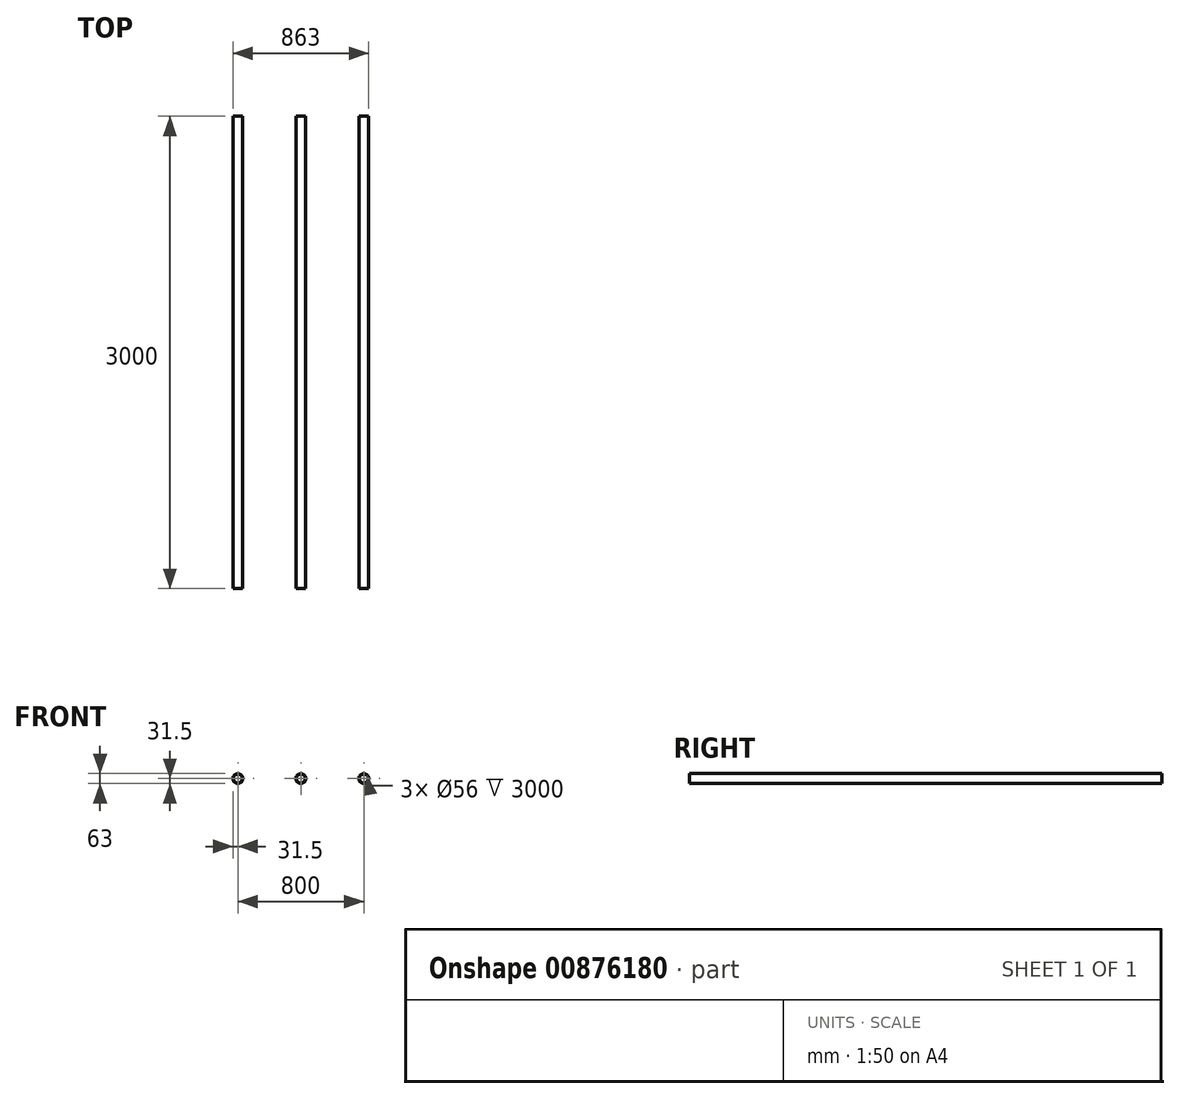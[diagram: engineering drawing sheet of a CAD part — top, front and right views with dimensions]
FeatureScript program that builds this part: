
annotation { "Feature Type Name" : "Feature", "Feature Type Description" : "" }
export const myFeature = defineFeature(function(context is Context, id is Id, definition is map)
    precondition{}
    {
        {
            var Q0;
            Q0=qCreatedBy(makeId("Front.planeOp"),FACE);
            var sketch = newSketch(context, id + "F0", { "sketchPlane" : qUnion([Q0])});
            skCircle(sketch, "E0", {"center": v(0, 0) * mm, "radius": 31.5 * mm});
            skCircle(sketch, "E1", {"center": v(0, 0) * mm, "radius": 28 * mm});
            skCircle(sketch, "E2", {"center": v(400, 0) * mm, "radius": 31.5 * mm});
            skCircle(sketch, "E3", {"center": v(400, 0) * mm, "radius": 28 * mm});
            skCircle(sketch, "E4", {"center": v(-400, 0) * mm, "radius": 31.5 * mm});
            skCircle(sketch, "E5", {"center": v(-400, 0) * mm, "radius": 28 * mm});
            skSolve(sketch);
        }
        {
            var Q0;
            Q0=makeQuery(id+"F0.imprint","IMPRINT",FACE,{"disambiguationData":[TD([[makeQuery(id+"F0.imprint","IMPRINT",EDGE,{"derivedFrom":sQuery(id+"F0.wireOp",EDGE,"E4")}),1.0]])]});
            var Q1;
            Q1=makeQuery(id+"F0.imprint","IMPRINT",FACE,{"disambiguationData":[TD([[makeQuery(id+"F0.imprint","IMPRINT",EDGE,{"derivedFrom":sQuery(id+"F0.wireOp",EDGE,"E0")}),1.0]])]});
            var Q2;
            Q2=makeQuery(id+"F0.imprint","IMPRINT",FACE,{"disambiguationData":[TD([[makeQuery(id+"F0.imprint","IMPRINT",EDGE,{"derivedFrom":sQuery(id+"F0.wireOp",EDGE,"E2")}),1.0]])]});
            extrude(context, id + "F1", {"entities" : qUnion([Q0, Q1, Q2]), "depth" : 3000 * mm, "offsetDistance" : 25 * mm});
        }
    });
